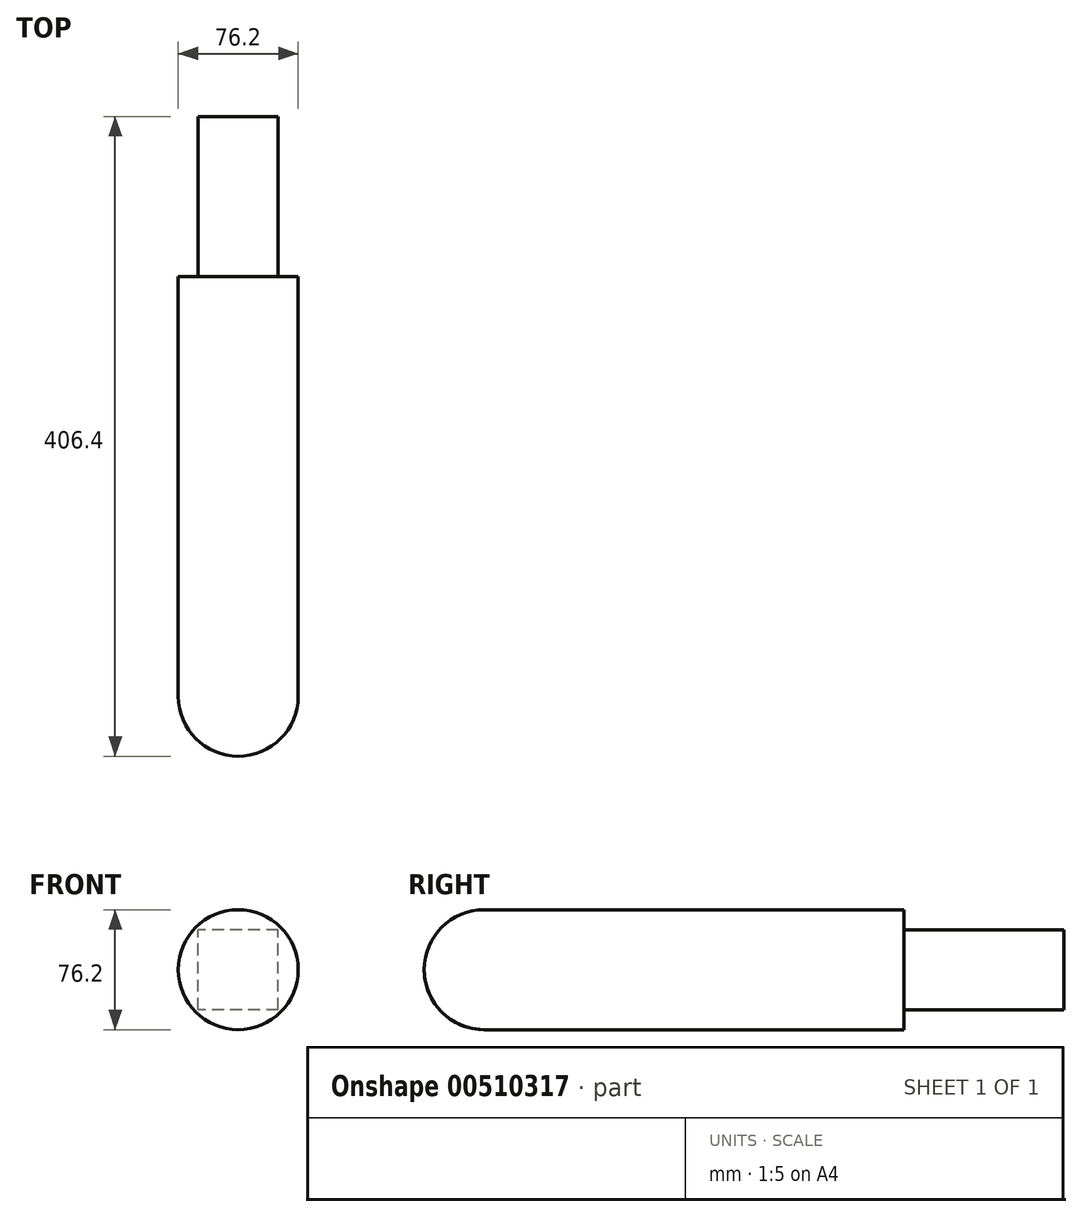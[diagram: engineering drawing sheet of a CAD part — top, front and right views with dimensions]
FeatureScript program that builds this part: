
annotation { "Feature Type Name" : "Feature", "Feature Type Description" : "" }
export const myFeature = defineFeature(function(context is Context, id is Id, definition is map)
    precondition{}
    {
        {
            var Q0;
            Q0=qCreatedBy(makeId("Front.planeOp"),FACE);
            var sketch = newSketch(context, id + "F0", { "sketchPlane" : qUnion([Q0])});
            skLineSegment(sketch, "E0.bottom", {"start": v(25.4, -25.4) * mm, "end": v(-25.4, -25.4) * mm});
            skLineSegment(sketch, "E0.top", {"start": v(25.4, 25.4) * mm, "end": v(-25.4, 25.4) * mm});
            skLineSegment(sketch, "E0.left", {"start": v(25.4, -25.4) * mm, "end": v(25.4, 25.4) * mm});
            skLineSegment(sketch, "E0.right", {"start": v(-25.4, -25.4) * mm, "end": v(-25.4, 25.4) * mm});
            skPoint(sketch, "E0.middle", {"position": v(0, 0) * mm});
            skSolve(sketch);
        }
        {
            var Q0;
            Q0=makeQuery(id+"F0.imprint","IMPRINT",FACE,{"disambiguationData":[TD([[makeQuery(id+"F0.imprint","IMPRINT",EDGE,{"derivedFrom":sQuery(id+"F0.wireOp",EDGE,"E0.bottom")}),-1.0]])]});
            extrude(context, id + "F1", {"entities" : qUnion([Q0]), "depth" : 101.6 * mm, "offsetDistance" : 25.4 * mm});
        }
        {
            var Q0;
            Q0=makeQuery(id+"F1.opExtrude","CAP_FACE",FACE,{"disambiguationData":[OSD([sQuery(id+"F0.wireOp",EDGE,"E0.bottom"),sQuery(id+"F0.wireOp",EDGE,"E0.top"),sQuery(id+"F0.wireOp",EDGE,"E0.left"),sQuery(id+"F0.wireOp",EDGE,"E0.right")])],"isStart":false});
            var sketch = newSketch(context, id + "F2", { "sketchPlane" : qUnion([Q0])});
            skCircle(sketch, "E1", {"center": v(0, 0) * mm, "radius": 38.1 * mm});
            skSolve(sketch);
        }
        {
            var Q0;
            Q0 = qSketchRegion(id + "F2", true);
            extrude(context, id + "F3", {"entities" : qUnion([Q0]), "operationType" : NewBodyOperationType.ADD, "depth" : 304.8 * mm, "offsetDistance" : 25.4 * mm});
        }
        {
            var Q0;
            Q0=makeQuery(id+"F3.opExtrude","CAP_EDGE",EDGE,{"disambiguationData":[OSD([sQuery(id+"F2.wireOp",EDGE,"E1")])],"isStart":false});
            fillet(context, id + "F4", {"entities" : qUnion([Q0]), "radius" : 38.1 * mm, "tangentPropagation" : true, "allowEdgeOverflow" : false});
        }
    });
